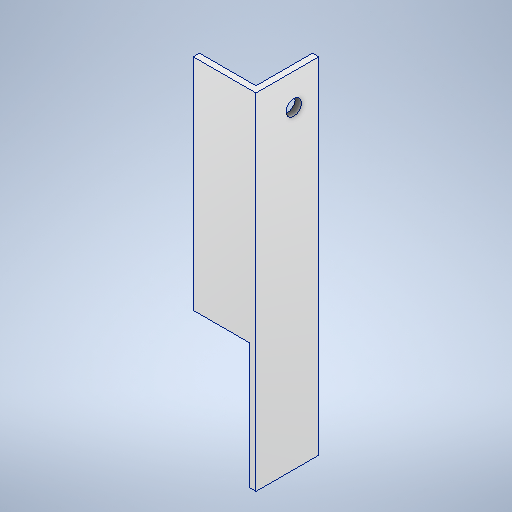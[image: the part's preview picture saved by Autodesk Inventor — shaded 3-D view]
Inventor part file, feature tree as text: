
AUTODESK INVENTOR PART (.ipt)
format: ipt  version: 2025 (Build 290162000, 162)  size: 268,800 bytes
history: native  units: mm
features: sketch x3, extrude x2, projected_geometry x2, other x1, hole x1
ambient origin geometry x8: Origin, YZ Plane, XZ Plane, XY Plane, X Axis, Y Axis, Z Axis, Center Point
bodies: Body1 (feature_tree)
feature tree (9):
  other  "Těleso1"
  extrude  "Vysunutí1"  Depth=10.0mm
  hole  "Díra1"  [1 undecoded]
  extrude  "Vysunutí2"  Depth=9.0mm
  sketch  "Náčrt1"
  sketch  "Náčrt2"
  projected_geometry  "Promítnutá smyčka1"
  sketch  "Náčrt3"
  projected_geometry  "Promítnutá smyčka2"
note: 1 required parameter value undecoded (feature->parameter linkage not recoverable at this tier; creation-order binding heuristic only, values carry confidence <= 0.55)
